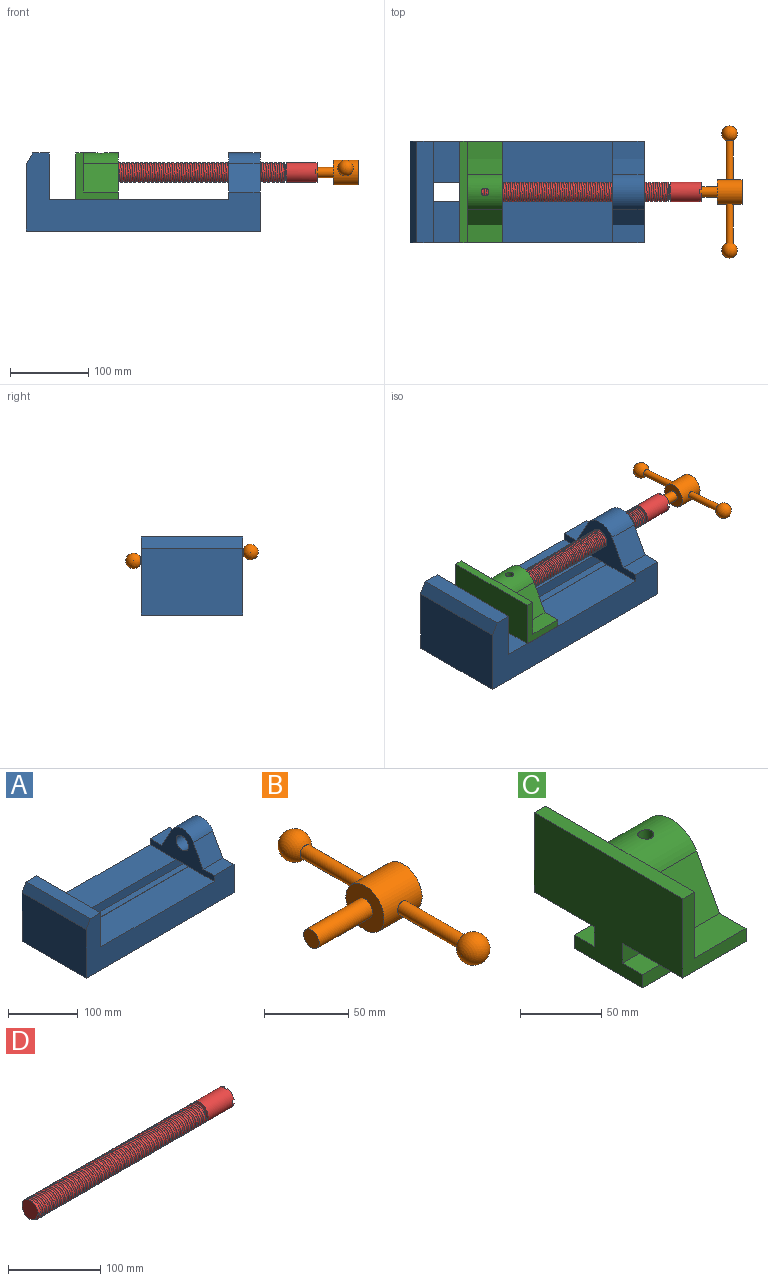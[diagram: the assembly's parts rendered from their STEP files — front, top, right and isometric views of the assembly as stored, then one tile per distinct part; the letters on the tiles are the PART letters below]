
ASSEMBLY  parts=4 mates=3
PART A: 28 faces, bbox 300x130x100 mm
  f0: plane 130x100mm, normal (1,0,0), area 7432.5mm2, adj f2,f7,f8,f10,f11,f12,f13,f14
  f1: plane 230x52.5mm, normal (0,0,1), area 12075mm2, adj f4,f7,f16,f21
  f2: plane 300x130mm, normal (0,0,-1), area 32250mm2, adj f0,f4,f6,f7,f8,f25,f26
  f3: plane 230x52.5mm, normal (0,0,1), area 12075mm2, adj f4,f8,f16,f19
  f4: plane 130x100mm, normal (1,0,0), area 9150mm2, adj f1,f2,f3,f5,f7,f8,f17,f18
  f5: plane 130x21.34mm, normal (0,0,1), area 2774.2mm2, adj f4,f7,f8,f9
  f6: plane 130x85mm, normal (-1,0,0), area 11050mm2, adj f2,f7,f8,f9
  f7: plane 300x100mm, normal (0,-1,0), area 14135mm2, adj f0,f1,f2,f4,f5,f6,f9,f10
  f8: plane 300x100mm, normal (0,1,0), area 14135mm2, adj f0,f2,f3,f4,f5,f6,f9,f11
  f9: plane 130x15mm, normal (-0.87,0,0.5), area 2251.7mm2, adj f5,f6,f7,f8
  f10: plane 40x22.94mm, normal (0,0,1), area 917.6mm2, adj f0,f7,f15,f16
  f11: plane 40x22.94mm, normal (0,0,1), area 917.6mm2, adj f0,f8,f12,f16
  f12: plane 40x36.95mm, normal (0,0.88,0.48), area 1682.4mm2, adj f0,f11,f13,f16
  f13: cylinder r=25mm len=43.92mm, axis (1,0,0), area 2145.1mm2, adj f0,f12,f15,f16
  f14: cylinder r=12.5mm len=40mm, axis (1,0,0), area 3141.6mm2, adj f0,f16
  f15: plane 40x36.95mm, normal (0,-0.88,0.48), area 1682.4mm2, adj f0,f10,f13,f16
  f16: plane 130x60mm, normal (-1,0,0), area 3582.5mm2, adj f1,f3,f7,f8,f10,f11,f12,f13
  f17: plane 270x10mm, normal (0,-1,0), area 2700mm2, adj f0,f4,f18,f27
  f18: plane 270x17.5mm, normal (0,0,-1), area 4725mm2, adj f0,f4,f17,f19
  f19: plane 270x15mm, normal (0,-1,0), area 4050mm2, adj f0,f3,f4,f18,f20
  f20: plane 40x25mm, normal (0,0,-1), area 1000mm2, adj f0,f16,f19,f21
  f21: plane 270x15mm, normal (0,1,0), area 4050mm2, adj f0,f1,f4,f20,f22
  f22: plane 270x17.5mm, normal (0,0,-1), area 4725mm2, adj f0,f4,f21,f23
  f23: plane 270x10mm, normal (0,1,0), area 2700mm2, adj f0,f4,f22,f24
  f24: plane 270x17.5mm, normal (0,0,1), area 4725mm2, adj f0,f4,f23,f25
  f25: plane 270x15mm, normal (0,1,0), area 4050mm2, adj f0,f2,f4,f24
  f26: plane 270x15mm, normal (0,-1,0), area 4050mm2, adj f0,f2,f4,f27
  f27: plane 270x17.5mm, normal (0,0,1), area 4725mm2, adj f0,f4,f17,f26
PART B: 9 faces, bbox 77x170x32 mm
  f0: cylinder r=4.5mm len=50.72mm, axis (0,1,0), area 1424.8mm2, adj f2,f8
  f1: cylinder r=4.5mm len=50.72mm, axis (0,1,0), area 1424.8mm2, adj f2,f7
  f2: cylinder r=16mm len=32mm, axis (-1,0,0), area 3088.5mm2, adj f0,f1,f5,f6
  f3: cylinder r=6.5mm len=45mm, axis (-1,0,0), area 1837.8mm2, adj f4,f6
  f4: plane 13x13mm, normal (-1,0,0), area 132.7mm2, adj f3
  f5: plane 32x32mm, normal (1,0,0), area 804.2mm2, adj f2
  f6: plane 32x32mm, normal (-1,0,0), area 671.5mm2, adj f2,f3
  f7: sphere r=10mm, area 1189.4mm2, adj f1
  f8: sphere r=10mm, area 1189.4mm2, adj f0
PART C: 24 faces, bbox 55x130x85 mm
  f0: cylinder r=12.5mm len=45mm, axis (1,0,0), area 3454.2mm2, adj f6,f15,f23
  f1: plane 55x52.5mm, normal (0,0,-1), area 2887.5mm2, adj f5,f6,f11,f17
  f2: plane 45x22.94mm, normal (0,0,1), area 1032.3mm2, adj f4,f6,f8,f14
  f3: plane 65x50mm, normal (1,0,0), area 1863.3mm2, adj f5,f7,f10,f12,f13
  f4: plane 65x50mm, normal (1,0,0), area 1863.3mm2, adj f2,f8,f10,f13,f14
  f5: plane 60x55mm, normal (0,1,0), area 1050mm2, adj f1,f3,f6,f7,f10,f11
  f6: plane 130x85mm, normal (1,0,0), area 4557.5mm2, adj f0,f1,f2,f5,f7,f8,f9,f12
  f7: plane 45x22.94mm, normal (0,0,1), area 1032.3mm2, adj f3,f5,f6,f12
  f8: plane 60x55mm, normal (0,-1,0), area 1050mm2, adj f2,f4,f6,f9,f10,f11
  f9: plane 55x52.5mm, normal (0,0,-1), area 2887.5mm2, adj f6,f8,f11,f18
  f10: plane 130x10mm, normal (0,0,1), area 1300mm2, adj f3,f4,f5,f8,f11
  f11: plane 130x85mm, normal (-1,0,0), area 8775mm2, adj f1,f5,f8,f9,f10,f16,f17,f18
  f12: plane 45x36.95mm, normal (0,0.88,0.48), area 1892.7mm2, adj f3,f6,f7,f13
  f13: cylinder r=25mm len=45mm, axis (1,0,0), area 2334.5mm2, adj f3,f4,f6,f12,f14,f23
  f14: plane 45x36.95mm, normal (0,-0.88,0.48), area 1892.7mm2, adj f2,f4,f6,f13
  f15: plane 25x25mm, normal (1,0,0), area 490.9mm2, adj f0
  f16: plane 55x17.5mm, normal (0,0,1), area 962.5mm2, adj f6,f11,f17,f22
  f17: plane 55x15mm, normal (0,1,0), area 825mm2, adj f1,f6,f11,f16
  f18: plane 55x15mm, normal (0,-1,0), area 825mm2, adj f6,f9,f11,f19
  f19: plane 55x17.5mm, normal (0,0,1), area 962.5mm2, adj f6,f11,f18,f20
  f20: plane 55x10mm, normal (0,-1,0), area 550mm2, adj f6,f11,f19,f21
  f21: plane 60x55mm, normal (0,0,-1), area 3300mm2, adj f6,f11,f20,f22
  f22: plane 55x10mm, normal (0,1,0), area 550mm2, adj f6,f11,f16,f21
  f23: cylinder r=5mm len=13.54mm, axis (0,0,1), area 401mm2, adj f0,f13
PART D: 27 faces, bbox 302x25.6x29.4 mm
  f0: plane 6.52x5.08mm, normal (1,0,0), area 30.9mm2, adj f3,f17,f18,f25
  f1: plane 6.52x5.08mm, normal (1,0,0), area 30.9mm2, adj f3,f19,f20,f25
  f2: plane 6.52x5.08mm, normal (1,0,0), area 30.9mm2, adj f3,f21,f22,f25
  f3: cylinder r=12.5mm len=40mm, axis (-1,0,0), area 3090.4mm2, adj f0,f1,f2,f4,f5,f6,f8,f10
  f4: plane 9.7x9.7mm, normal (1,0,0), area 58.6mm2, adj f3,f16,f17,f25
  f5: plane 9.7x9.7mm, normal (1,0,0), area 58.6mm2, adj f3,f18,f19,f25
  f6: plane 9.7x9.7mm, normal (1,0,0), area 58.6mm2, adj f3,f22,f23,f25
  f7: cone r=10mm half-angle=75.4deg, axis (-1,0,0), area 167.7mm2, adj f9,f12,f14,f15
  f8: plane 9.7x9.7mm, normal (1,0,0), area 58.6mm2, adj f3,f20,f21,f25
  f9: cylinder r=10mm len=20mm, axis (1,0,0), area 75.4mm2, adj f7,f10
  f10: cone r=12.5mm half-angle=75.4deg, axis (1,0,0), area 182.6mm2, adj f3,f9
  f11: plane 25x24.97mm, normal (-1,0,0), area 467.8mm2, adj f12,f13,f15
  f12: cylinder r=12.5mm len=257.5mm, axis (-1,0,0), area 4870.6mm2, adj f7,f11,f13,f14,f15
  f13: plane 1.93x1.92mm, normal (0.07,0,-1), area 1.8mm2, adj f11,f12,f15
  f14: plane 2.37x2mm, normal (-0.07,0,1), area 2.1mm2, adj f7,f12,f15
  f15: bspline ~260.49x28.87mm, area 15387mm2, adj f7,f11,f12,f13,f14
  f16: plane 6.26x2.5mm, normal (0,-1,0), area 15.6mm2, adj f3,f4,f24,f25
  f17: plane 6.26x2.5mm, normal (0,0,1), area 15.6mm2, adj f0,f3,f4,f25
  f18: plane 6.26x2.5mm, normal (0,0,-1), area 15.6mm2, adj f0,f3,f5,f25
  f19: plane 6.26x2.5mm, normal (0,-1,0), area 15.6mm2, adj f1,f3,f5,f25
  f20: plane 6.26x2.5mm, normal (0,1,0), area 15.6mm2, adj f1,f3,f8,f25
  f21: plane 6.26x2.5mm, normal (0,0,-1), area 15.6mm2, adj f2,f3,f8,f25
  f22: plane 6.26x2.5mm, normal (0,0,1), area 15.6mm2, adj f2,f3,f6,f25
  f23: plane 6.26x2.5mm, normal (0,1,0), area 15.6mm2, adj f3,f6,f24,f25
  f24: plane 6.52x5.08mm, normal (1,0,0), area 30.9mm2, adj f3,f16,f23,f25
  f25: cylinder r=6.5mm len=25mm, axis (1,0,0), area 968.8mm2, adj f0,f1,f2,f4,f5,f6,f8,f16
  f26: plane 13x13mm, normal (1,0,0), area 132.7mm2, adj f25
PLACE A t=(7.95,-18.82,4.96)mm fixed
PLACE B rot(axis=(-1,0,0),4.4deg) t=(41.52,-24.52,5.18)mm
PLACE C t=(41.52,-18.82,4.96)mm
PLACE D rot(axis=(1,0,0),85.6deg) t=(41.52,55.97,74.26)mm
MATE revolute D.f9 <-> C.f0  axis (-1,0,0) through (-218.48,-18.82,79.96)mm
MATE fastened B.f3 <-> D.f9  axis (-1,0,0) through (56.52,-18.82,79.96)mm
MATE slider C.f11 <-> A.f4  axis (1,0,0) through (-228.48,46.18,44.96)mm
